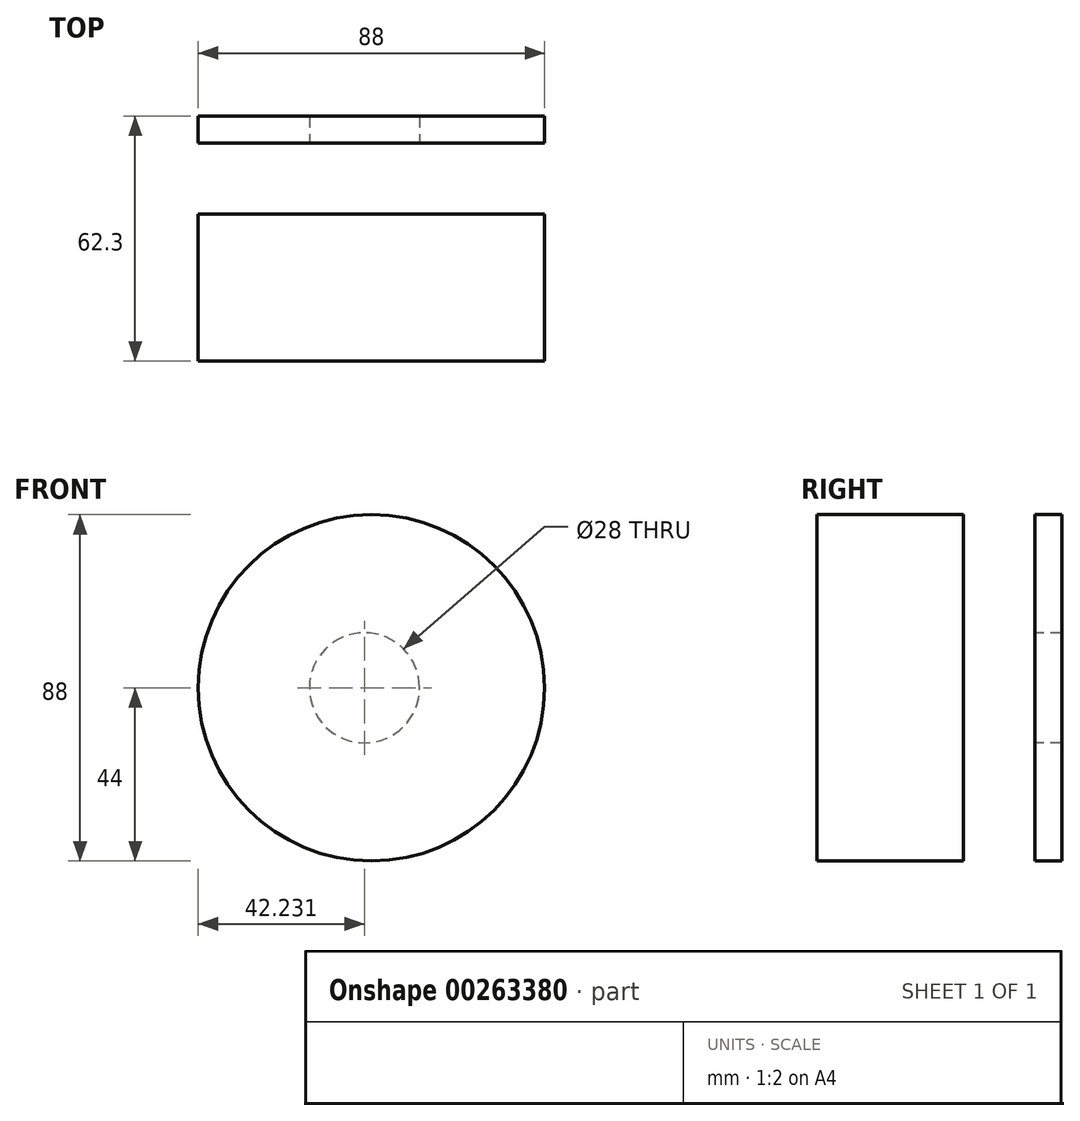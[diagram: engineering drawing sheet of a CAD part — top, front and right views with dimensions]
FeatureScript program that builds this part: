
annotation { "Feature Type Name" : "Feature", "Feature Type Description" : "" }
export const myFeature = defineFeature(function(context is Context, id is Id, definition is map)
    precondition{}
    {
        {
            var Q0;
            Q0=qCreatedBy(makeId("Front.planeOp"),FACE);
            var sketch = newSketch(context, id + "F0", { "sketchPlane" : qUnion([Q0])});
            skCircle(sketch, "E0", {"center": v(0, 0) * mm, "radius": 44 * mm});
            skSolve(sketch);
        }
        {
            var Q0;
            Q0=makeQuery(id+"F0.imprint","IMPRINT",FACE,{"disambiguationData":[TD([[makeQuery(id+"F0.imprint","IMPRINT",EDGE,{"derivedFrom":sQuery(id+"F0.wireOp",EDGE,"E0")}),1.0]])]});
            extrude(context, id + "F1", {"entities" : qUnion([Q0]), "oppositeDirection" : true, "depth" : 37.3 * mm});
        }
        {
            var Q0;
            Q0=makeQuery(id+"F1.opExtrude","CAP_FACE",FACE,{"disambiguationData":[OSD([sQuery(id+"F0.wireOp",EDGE,"E0")])],"isStart":true});
            var sketch = newSketch(context, id + "F2", { "sketchPlane" : qUnion([Q0])});
            skCircle(sketch, "E1", {"center": v(0, 0) * mm, "radius": 34 * mm});
            skSolve(sketch);
        }
        {
            var Q0;
            Q0=makeQuery(id+"F2.imprint","IMPRINT",FACE,{"disambiguationData":[TD([[makeQuery(id+"F2.imprint","IMPRINT",EDGE,{"derivedFrom":sQuery(id+"F2.wireOp",EDGE,"E1")}),1.0]])]});
            var Q1;
            Q1=sQuery(id+"F2.wireOp",EDGE,"E1");
            extrude(context, id + "F3", {"entities" : qUnion([Q0]), "bodyType" : ToolBodyType.SURFACE, "surfaceEntities" : qUnion([Q1]), "oppositeDirection" : true, "depth" : 55.2 * mm, "hasSecondDirection" : true, "secondDirectionOppositeDirection" : true, "secondDirectionDepth" : 8.8 * mm});
        }
        {
            var Q0;
            Q0=makeQuery(id+"F1.opExtrude","CAP_FACE",FACE,{"disambiguationData":[OSD([sQuery(id+"F0.wireOp",EDGE,"E0")])],"isStart":false});
            var sketch = newSketch(context, id + "F4", { "sketchPlane" : qUnion([Q0])});
            skCircle(sketch, "E2", {"center": v(1.77, 0) * mm, "radius": 14 * mm});
            skSolve(sketch);
        }
        {
            var Q0;
            Q0=makeQuery(id+"F4.imprint","IMPRINT",FACE,{"disambiguationData":[TD([[makeQuery(id+"F4.imprint","IMPRINT",EDGE,{"derivedFrom":sQuery(id+"F4.wireOp",EDGE,"E2")}),-1.0]])]});
            extrude(context, id + "F5", {"entities" : qUnion([Q0]), "depth" : 25 * mm, "hasSecondDirection" : true, "secondDirectionOppositeDirection" : false, "secondDirectionDepth" : 18.1 * mm});
        }
    });
